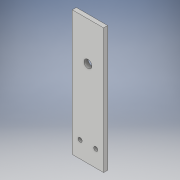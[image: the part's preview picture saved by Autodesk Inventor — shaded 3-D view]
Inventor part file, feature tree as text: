
AUTODESK INVENTOR PART (.ipt)
format: ipt  version: 2018 (Build 220112000, 112)  size: 103,936 bytes
history: native  units: in
note: dims shown in document units (in); Inventor stores cm internally (conversion verified against a paired STEP export)
features: sketch x2, extrude x1, hole x1
ambient origin geometry x8: Origin, YZ Plane, XZ Plane, XY Plane, X Axis, Y Axis, Z Axis, Center Point
bodies: Solid1 (feature_tree)
feature tree (4):
  extrude  "Extrusion1"  Depth=7.874in
  hole  "Hole1"  [1 undecoded]
  sketch  "Sketch1"  dims[d0=1.9685in d1=7.874in]
  sketch  "Sketch3"  dims[d2=0.2559in d3=0.2559in d4=0.2559in d5=0.0in d7=0.5in d8=0.5in d9=0.2953in d10=0.1476in d11=0.0984in d12=90.0deg d13=0.3937in d14=0.8108in]
note: 1 required parameter value undecoded (feature->parameter linkage not recoverable at this tier; creation-order binding heuristic only, values carry confidence <= 0.55)
